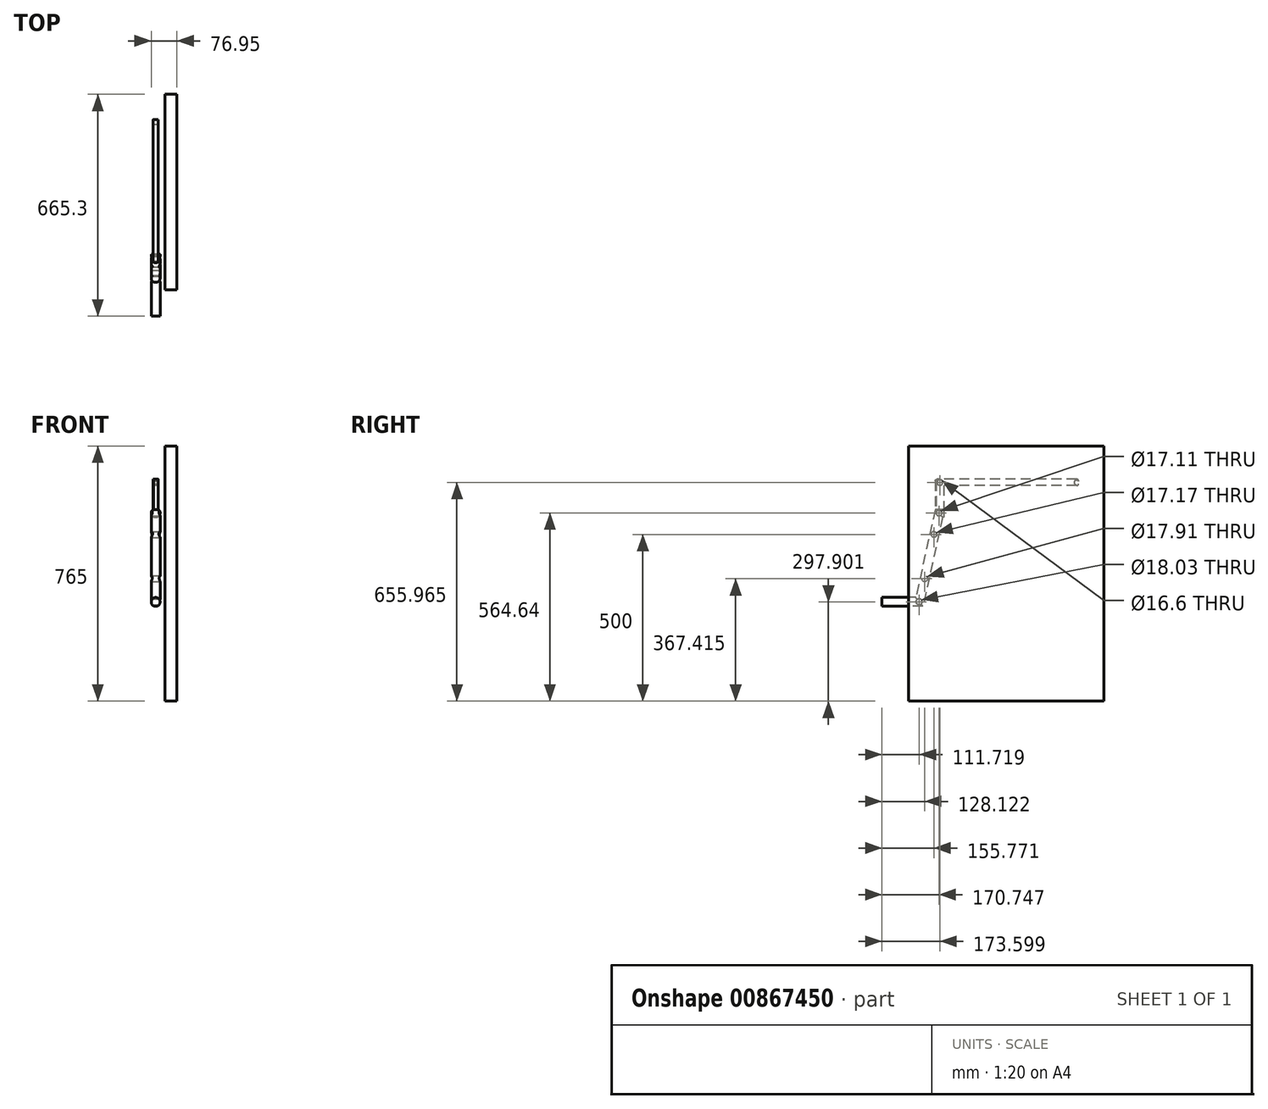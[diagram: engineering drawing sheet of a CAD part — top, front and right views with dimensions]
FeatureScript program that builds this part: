
annotation { "Feature Type Name" : "Feature", "Feature Type Description" : "" }
export const myFeature = defineFeature(function(context is Context, id is Id, definition is map)
    precondition{}
    {
        {
            var Q0;
            Q0=qCreatedBy(makeId("Front.planeOp"),FACE);
            var sketch = newSketch(context, id + "F0", { "sketchPlane" : qUnion([Q0])});
            skCircle(sketch, "E0", {"center": v(0, 64.42) * mm, "radius": 13.3 * mm});
            skSolve(sketch);
        }
        {
            var Q0;
            Q0=qCreatedBy(makeId("Right.planeOp"),FACE);
            var sketch = newSketch(context, id + "F1", { "sketchPlane" : qUnion([Q0])});
            skLineSegment(sketch, "E1", {"start": v(0, 64.42) * mm, "end": v(-13.95, 64.42) * mm});
            skLineSegment(sketch, "E2", {"start": v(-13.95, 64.42) * mm, "end": v(-73.19, -202.2) * mm});
            skLineSegment(sketch, "E3", {"start": v(-73.19, -202.2) * mm, "end": v(-185.05, -202.2) * mm});
            skSolve(sketch);
        }
        {
            var Q0;
            Q0=makeQuery(id+"F0.imprint","IMPRINT",FACE,{"disambiguationData":[TD([[makeQuery(id+"F0.imprint","IMPRINT",EDGE,{"derivedFrom":sQuery(id+"F0.wireOp",EDGE,"E0")}),1.0]])]});
            var Q1;
            Q1=sQuery(id+"F1.wireOp",EDGE,"E1");
            var Q2;
            Q2=sQuery(id+"F1.wireOp",EDGE,"E2");
            var Q3;
            Q3=sQuery(id+"F1.wireOp",EDGE,"E3");
            sweep(context, id + "F2", {"profiles" : qUnion([Q0]), "path" : qUnion([Q1, Q2, Q3])});
        }
        {
            var Q0;
            Q0=qCreatedBy(makeId("Top.planeOp"),FACE);
            var sketch = newSketch(context, id + "F3", { "sketchPlane" : qUnion([Q0])});
            skLineSegment(sketch, "E4.bottom", {"start": v(27.62, -105.68) * mm, "end": v(63.64, -105.68) * mm});
            skLineSegment(sketch, "E4.top", {"start": v(27.62, 480.25) * mm, "end": v(63.64, 480.25) * mm});
            skLineSegment(sketch, "E4.left", {"start": v(27.62, -105.68) * mm, "end": v(27.62, 480.25) * mm});
            skLineSegment(sketch, "E4.right", {"start": v(63.64, -105.68) * mm, "end": v(63.64, 480.25) * mm});
            skSolve(sketch);
        }
        {
            var Q0;
            Q0=makeQuery(id+"F3.imprint","IMPRINT",FACE,{"disambiguationData":[TD([[makeQuery(id+"F3.imprint","IMPRINT",EDGE,{"derivedFrom":sQuery(id+"F3.wireOp",EDGE,"E4.bottom")}),1.0]])]});
            extrude(context, id + "F4", {"entities" : qUnion([Q0]), "oppositeDirection" : true, "depth" : 500 * mm, "offsetDistance" : 25 * mm, "hasSecondDirection" : true, "secondDirectionOppositeDirection" : false, "secondDirectionDepth" : 95 * mm});
        }
        {
            var Q0;
            Q0=makeQuery(id+"F4.opExtrude","SWEPT_FACE",FACE,{"disambiguationData":[OSD([sQuery(id+"F3.wireOp",EDGE,"E4.left")])]});
            var sketch = newSketch(context, id + "F5", { "sketchPlane" : qUnion([Q0])});
            skCircle(sketch, "E5", {"center": v(73.33, -202.1) * mm, "radius": 9.02 * mm});
            skCircle(sketch, "E6", {"center": v(14.3, 64.64) * mm, "radius": 8.55 * mm});
            skCircle(sketch, "E7", {"center": v(56.93, -132.59) * mm, "radius": 8.96 * mm});
            skCircle(sketch, "E8", {"center": v(29.28, 0) * mm, "radius": 8.59 * mm});
            skSolve(sketch);
        }
        {
            var Q0;
            Q0 = qSketchRegion(id + "F5", true);
            extrude(context, id + "F6", {"entities" : qUnion([Q0]), "depth" : 80 * mm, "offsetDistance" : 25 * mm});
        }
        {
            var Q0;
            Q0=makeQuery(id+"F6.opExtrude","SWEPT_BODY",BODY,{"disambiguationData":[OSD([sQuery(id+"F5.wireOp",EDGE,"E8")])]});
            var Q1;
            Q1=makeQuery(id+"F6.opExtrude","SWEPT_BODY",BODY,{"disambiguationData":[OSD([sQuery(id+"F5.wireOp",EDGE,"E7")])]});
            var Q2;
            Q2=makeQuery(id+"F6.opExtrude","SWEPT_BODY",BODY,{"disambiguationData":[OSD([sQuery(id+"F5.wireOp",EDGE,"E5")])]});
            var Q3;
            Q3=makeQuery(id+"F6.opExtrude","SWEPT_BODY",BODY,{"disambiguationData":[OSD([sQuery(id+"F5.wireOp",EDGE,"E6")])]});
            var Q4;
            Q4=makeQuery(id+"F2.opSweep","SWEPT_BODY",BODY,{"disambiguationData":[OSD([sQuery(id+"F0.wireOp",EDGE,"E0"),sQuery(id+"F1.wireOp",EDGE,"E3")])]});
            booleanBodies(context, id + "F7", {"operationType" : BooleanOperationType.SUBTRACTION, "tools" : qUnion([Q0, Q1, Q2, Q3]), "targets" : qUnion([Q4])});
        }
        {
            var Q0;
            Q0=qCreatedBy(makeId("Front.planeOp"),FACE);
            var sketch = newSketch(context, id + "F8", { "sketchPlane" : qUnion([Q0])});
            skLineSegment(sketch, "E9.bottom", {"start": v(36.32, 99.43) * mm, "end": v(-26.38, 99.43) * mm});
            skLineSegment(sketch, "E9.top", {"start": v(36.32, 75) * mm, "end": v(-26.38, 75) * mm});
            skLineSegment(sketch, "E9.left", {"start": v(36.32, 99.43) * mm, "end": v(36.32, 75) * mm});
            skLineSegment(sketch, "E9.right", {"start": v(-26.38, 99.43) * mm, "end": v(-26.38, 75) * mm});
            skSolve(sketch);
        }
        {
            var Q0;
            Q0=makeQuery(id+"F8.imprint","IMPRINT",FACE,{"disambiguationData":[TD([[makeQuery(id+"F8.imprint","IMPRINT",EDGE,{"derivedFrom":sQuery(id+"F8.wireOp",EDGE,"E9.bottom")}),1.0]])]});
            extrude(context, id + "F9", {"entities" : qUnion([Q0]), "depth" : 30.8 * mm, "offsetDistance" : 25 * mm});
        }
        {
            var Q0;
            Q0=makeQuery(id+"F9.opExtrude","SWEPT_BODY",BODY,{"disambiguationData":[OSD([sQuery(id+"F8.wireOp",EDGE,"E9.bottom"),sQuery(id+"F8.wireOp",EDGE,"E9.top"),sQuery(id+"F8.wireOp",EDGE,"E9.left"),sQuery(id+"F8.wireOp",EDGE,"E9.right")])]});
            var Q1;
            Q1=makeQuery(id+"F2.opSweep","SWEPT_BODY",BODY,{"disambiguationData":[OSD([sQuery(id+"F0.wireOp",EDGE,"E0"),sQuery(id+"F1.wireOp",EDGE,"E3")])]});
            booleanBodies(context, id + "F10", {"operationType" : BooleanOperationType.SUBTRACTION, "tools" : qUnion([Q0]), "targets" : qUnion([Q1])});
        }
        {
            var Q0;
            Q0=makeQuery(id+"F10.opBoolean","COPY",FACE,{"derivedFrom":makeQuery(id+"F9.opExtrude","SWEPT_FACE",FACE,{"disambiguationData":[OSD([sQuery(id+"F8.wireOp",EDGE,"E9.top")])]})});
            var sketch = newSketch(context, id + "F11", { "sketchPlane" : qUnion([Q0])});
            skCircle(sketch, "E10", {"center": v(0, -11.6) * mm, "radius": 13.54 * mm});
            skLineSegment(sketch, "E11.bottom", {"start": v(-8.07, 0) * mm, "end": v(8.07, 0) * mm});
            skLineSegment(sketch, "E11.top", {"start": v(-8.07, -22.43) * mm, "end": v(8.07, -22.43) * mm});
            skLineSegment(sketch, "E11.left", {"start": v(-8.07, 0) * mm, "end": v(-8.07, -22.43) * mm});
            skLineSegment(sketch, "E11.right", {"start": v(8.07, 0) * mm, "end": v(8.07, -22.43) * mm});
            skSolve(sketch);
        }
        {
            var Q0;
            {var subQ0=sQuery(id+"F11.wireOp",EDGE,"E11.top");Q0=makeQuery(id+"F11.imprint","IMPRINT",FACE,{"disambiguationData":[TD([[makeQuery(id+"F11.imprint","IMPRINT",EDGE,{"derivedFrom":subQ0}),1.0]])]});}
            var Q1;
            {var subQ4=sQuery(id+"F11.wireOp",EDGE,"E11.top");Q1=makeQuery(id+"F11.imprint","IMPRINT",FACE,{"disambiguationData":[TD([[makeQuery(id+"F11.imprint","IMPRINT",EDGE,{"derivedFrom":subQ4}),-1.0]])]});}
            var Q2;
            {var subQ0=sQuery(id+"F11.wireOp",EDGE,"E11.bottom");var subQ1=sQuery(id+"F11.wireOp",EDGE,"E10");var subQ2=makeQuery(id+"F11.imprint","INTERSECT",VERTEX,{"disambiguationData":[OD(0.0)],"derivedFrom":[subQ1,subQ0]});Q2=makeQuery(id+"F11.imprint","IMPRINT",FACE,{"disambiguationData":[TD([[makeQuery(id+"F11.imprint","IMPRINT",EDGE,{"disambiguationData":[TD([[subQ2,1.0]])],"derivedFrom":subQ1}),-1.0]])]});}
            var Q3;
            {var subQ0=sQuery(id+"F11.wireOp",EDGE,"E11.bottom");var subQ1=sQuery(id+"F11.wireOp",EDGE,"E10");var subQ2=makeQuery(id+"F11.imprint","INTERSECT",VERTEX,{"disambiguationData":[OD(1.0)],"derivedFrom":[subQ1,subQ0]});Q3=makeQuery(id+"F11.imprint","IMPRINT",FACE,{"disambiguationData":[TD([[makeQuery(id+"F11.imprint","IMPRINT",EDGE,{"disambiguationData":[TD([[subQ2,-1.0]])],"derivedFrom":subQ1}),-1.0]])]});}
            extrude(context, id + "F12", {"entities" : qUnion([Q0, Q1, Q2, Q3]), "operationType" : NewBodyOperationType.ADD, "depth" : 90.5 * mm, "offsetDistance" : 25 * mm});
        }
        {
            var Q0;
            Q0=makeQuery(id+"F12.boolean.opBoolean","MERGE",FACE,{"derivedFrom":[makeQuery(id+"F2.opSweep","CAP_FACE",FACE,{"disambiguationData":[OSD([sQuery(id+"F0.wireOp",EDGE,"E0"),sQuery(id+"F1.wireOp",VERTEX,"E1.start")])],"isStart":true}),makeQuery(id+"F12.opExtrude","SWEPT_FACE",FACE,{"disambiguationData":[OSD([sQuery(id+"F11.wireOp",EDGE,"E11.bottom")])]})]});
            var sketch = newSketch(context, id + "F13", { "sketchPlane" : qUnion([Q0])});
            skLineSegment(sketch, "E12.bottom", {"start": v(-8.07, 165.5) * mm, "end": v(8.07, 165.5) * mm});
            skLineSegment(sketch, "E12.top", {"start": v(-8.07, 146.61) * mm, "end": v(8.07, 146.61) * mm});
            skLineSegment(sketch, "E12.left", {"start": v(-8.07, 165.5) * mm, "end": v(-8.07, 146.61) * mm});
            skLineSegment(sketch, "E12.right", {"start": v(8.07, 165.5) * mm, "end": v(8.07, 146.61) * mm});
            skSolve(sketch);
        }
        {
            var Q0;
            Q0=makeQuery(id+"F13.imprint","IMPRINT",FACE,{"disambiguationData":[TD([[makeQuery(id+"F13.imprint","IMPRINT",EDGE,{"derivedFrom":sQuery(id+"F13.wireOp",EDGE,"E12.bottom")}),-1.0]])]});
            extrude(context, id + "F14", {"entities" : qUnion([Q0]), "operationType" : NewBodyOperationType.ADD, "depth" : 404 * mm, "offsetDistance" : 25 * mm});
        }
        {
            var Q0;
            Q0=makeQuery(id+"F3.imprint","IMPRINT",FACE,{"disambiguationData":[TD([[makeQuery(id+"F3.imprint","IMPRINT",EDGE,{"derivedFrom":sQuery(id+"F3.wireOp",EDGE,"E4.bottom")}),1.0]])]});
            extrude(context, id + "F15", {"entities" : qUnion([Q0]), "operationType" : NewBodyOperationType.ADD, "depth" : 265 * mm, "offsetDistance" : 25 * mm});
        }
        {
            var Q0;
            {var subQ0=sQuery(id+"F3.wireOp",EDGE,"E4.left");Q0=makeQuery(id+"F15.boolean.opBoolean","MERGE",FACE,{"derivedFrom":[makeQuery(id+"F4.opExtrude","SWEPT_FACE",FACE,{"disambiguationData":[OSD([subQ0])]}),makeQuery(id+"F15.opExtrude","SWEPT_FACE",FACE,{"disambiguationData":[OSD([subQ0])]})]});}
            var sketch = newSketch(context, id + "F16", { "sketchPlane" : qUnion([Q0])});
            skCircle(sketch, "E13", {"center": v(11.45, 155.97) * mm, "radius": 8.3 * mm});
            skCircle(sketch, "E14", {"center": v(-397.88, 155.86) * mm, "radius": 7.05 * mm});
            skSolve(sketch);
        }
        {
            var Q0;
            Q0 = qSketchRegion(id + "F16", true);
            extrude(context, id + "F17", {"entities" : qUnion([Q0]), "depth" : 50 * mm, "offsetDistance" : 25 * mm});
        }
        {
            var Q0;
            Q0=makeQuery(id+"F17.opExtrude","SWEPT_BODY",BODY,{"disambiguationData":[OSD([sQuery(id+"F16.wireOp",EDGE,"E14")])]});
            var Q1;
            Q1=makeQuery(id+"F17.opExtrude","SWEPT_BODY",BODY,{"disambiguationData":[OSD([sQuery(id+"F16.wireOp",EDGE,"E13")])]});
            var Q2;
            Q2=makeQuery(id+"F2.opSweep","SWEPT_BODY",BODY,{"disambiguationData":[OSD([sQuery(id+"F0.wireOp",EDGE,"E0"),sQuery(id+"F1.wireOp",EDGE,"E3")])]});
            booleanBodies(context, id + "F18", {"operationType" : BooleanOperationType.SUBTRACTION, "tools" : qUnion([Q0, Q1]), "targets" : qUnion([Q2])});
        }
        {
            var Q0;
            Q0=makeQuery(id+"F12.opExtrude","CAP_EDGE",EDGE,{"disambiguationData":[OSD([sQuery(id+"F11.wireOp",EDGE,"E10")])],"isStart":false});
            var Q1;
            Q1=makeQuery(id+"F14.opExtrude","CAP_EDGE",EDGE,{"disambiguationData":[OSD([sQuery(id+"F13.wireOp",EDGE,"E12.bottom")])],"isStart":false});
            var Q2;
            Q2=makeQuery(id+"F14.opExtrude","CAP_EDGE",EDGE,{"disambiguationData":[OSD([sQuery(id+"F13.wireOp",EDGE,"E12.top")])],"isStart":false});
            var Q3;
            Q3=makeQuery(id+"F14.opExtrude","CAP_EDGE",EDGE,{"disambiguationData":[OSD([sQuery(id+"F13.wireOp",EDGE,"E12.top")])],"isStart":true});
            fillet(context, id + "F19", {"entities" : qUnion([Q0, Q1, Q2, Q3]), "radius" : 5 * mm, "tangentPropagation" : true, "allowEdgeOverflow" : false});
        }
    });
